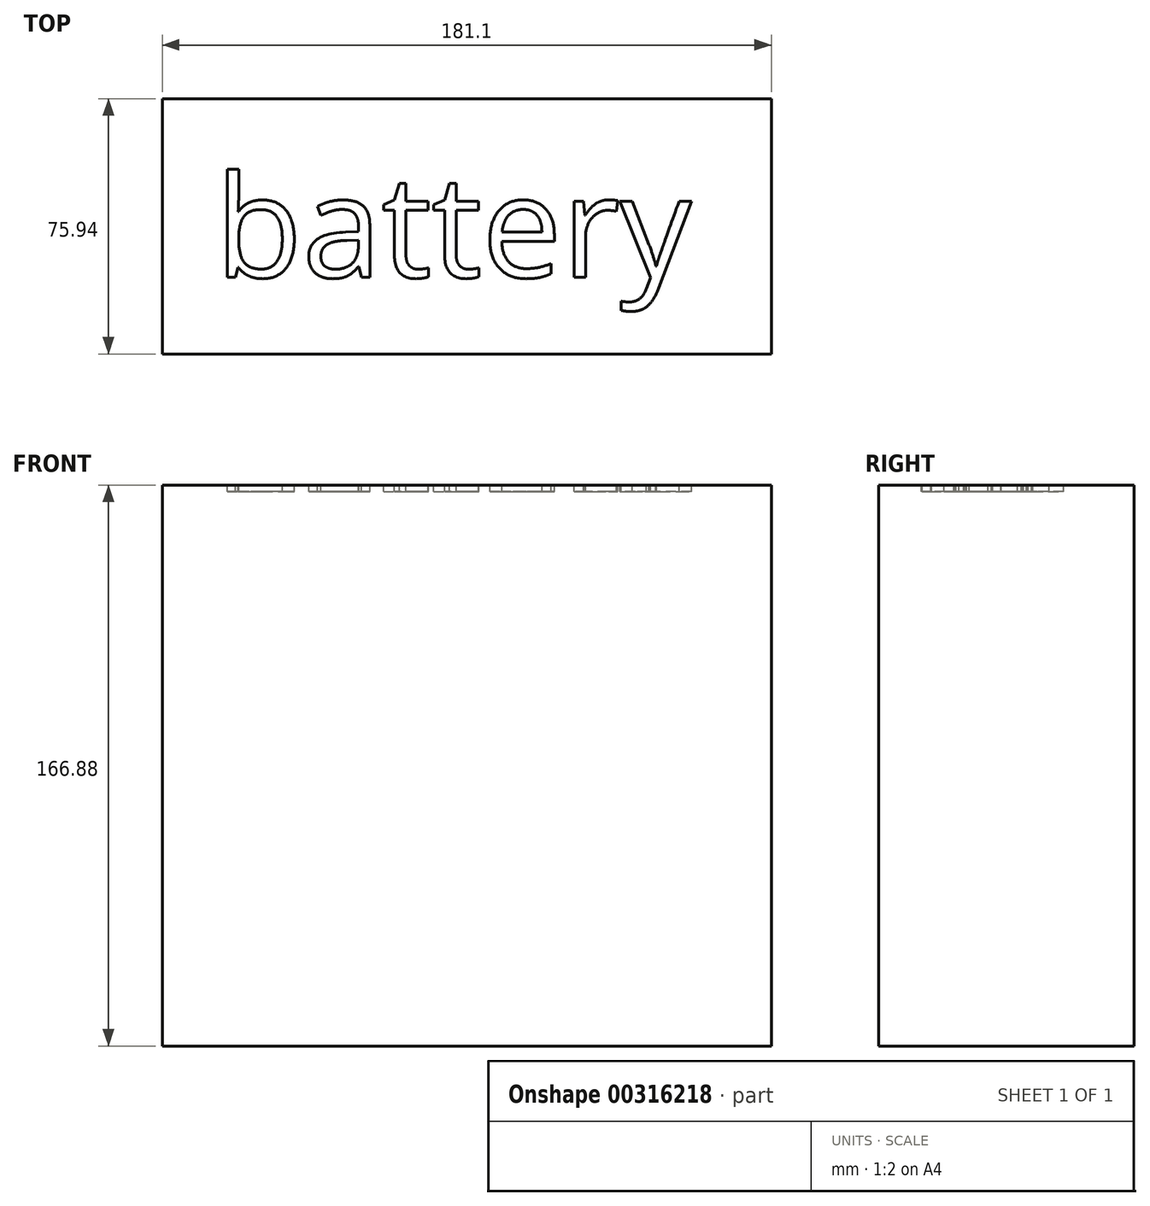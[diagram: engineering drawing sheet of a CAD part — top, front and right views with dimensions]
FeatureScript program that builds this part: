
annotation { "Feature Type Name" : "Feature", "Feature Type Description" : "" }
export const myFeature = defineFeature(function(context is Context, id is Id, definition is map)
    precondition{}
    {
        {
            var Q0;
            Q0=qCreatedBy(makeId("Top.planeOp"),FACE);
            var sketch = newSketch(context, id + "F0", { "sketchPlane" : qUnion([Q0])});
            skLineSegment(sketch, "E0.bottom", {"start": v(-90.55, 37.97) * mm, "end": v(90.55, 37.97) * mm});
            skLineSegment(sketch, "E0.top", {"start": v(-90.55, -37.97) * mm, "end": v(90.55, -37.97) * mm});
            skLineSegment(sketch, "E0.left", {"start": v(-90.55, 37.97) * mm, "end": v(-90.55, -37.97) * mm});
            skLineSegment(sketch, "E0.right", {"start": v(90.55, 37.97) * mm, "end": v(90.55, -37.97) * mm});
            skPoint(sketch, "E0.middle", {"position": v(0, 0) * mm});
            skSolve(sketch);
        }
        {
            var Q0;
            Q0 = qSketchRegion(id + "F0", true);
            extrude(context, id + "F1", {"entities" : qUnion([Q0]), "depth" : 166.88 * mm});
        }
        {
            var Q0;
            Q0=makeQuery(id+"F1.opExtrude","CAP_FACE",FACE,{"disambiguationData":[OSD([sQuery(id+"F0.wireOp",EDGE,"E0.bottom"),sQuery(id+"F0.wireOp",EDGE,"E0.top"),sQuery(id+"F0.wireOp",EDGE,"E0.left"),sQuery(id+"F0.wireOp",EDGE,"E0.right")])],"isStart":false});
            var sketch = newSketch(context, id + "F2", { "sketchPlane" : qUnion([Q0])});
            skLineSegment(sketch, "E1.0.0", {"start": v(-90.55, 37.97) * mm, "end": v(-90.55, -37.97) * mm});
            skLineSegment(sketch, "E1.0.1", {"start": v(-90.55, -37.97) * mm, "end": v(90.55, -37.97) * mm});
            skLineSegment(sketch, "E1.0.2", {"start": v(90.55, -37.97) * mm, "end": v(90.55, 37.97) * mm});
            skLineSegment(sketch, "E1.0.3", {"start": v(90.55, 37.97) * mm, "end": v(-90.55, 37.97) * mm});
            skText(sketch, "E2", { "text": "battery", "fontName": "OpenSans-Regular.ttf"});
            const initialGuessF2  = {"E2": [-0.07487, -0.0152, 1, 0, 0.03048]};
            skSetInitialGuess(sketch, initialGuessF2);
            skSolve(sketch);
        }
        {
            var Q0;
            Q0=makeQuery(id+"F2.imprint","IMPRINT",FACE,{"disambiguationData":[TD([[makeQuery(id+"F2.imprint","IMPRINT",EDGE,{"derivedFrom":sQuery(id+"F2.wireOp",EDGE,"E2.sketch_text.stroke-0")}),-1.0]])]});
            var Q1;
            Q1=makeQuery(id+"F2.imprint","IMPRINT",FACE,{"disambiguationData":[TD([[makeQuery(id+"F2.imprint","IMPRINT",EDGE,{"derivedFrom":sQuery(id+"F2.wireOp",EDGE,"E2.sketch_text.stroke-50")}),-1.0]])]});
            var Q2;
            Q2=makeQuery(id+"F2.imprint","IMPRINT",FACE,{"disambiguationData":[TD([[makeQuery(id+"F2.imprint","IMPRINT",EDGE,{"derivedFrom":sQuery(id+"F2.wireOp",EDGE,"E2.sketch_text.stroke-69")}),-1.0]])]});
            var Q3;
            Q3=makeQuery(id+"F2.imprint","IMPRINT",FACE,{"disambiguationData":[TD([[makeQuery(id+"F2.imprint","IMPRINT",EDGE,{"derivedFrom":sQuery(id+"F2.wireOp",EDGE,"E2.sketch_text.stroke-88")}),-1.0]])]});
            var Q4;
            Q4=makeQuery(id+"F2.imprint","IMPRINT",FACE,{"disambiguationData":[TD([[makeQuery(id+"F2.imprint","IMPRINT",EDGE,{"derivedFrom":sQuery(id+"F2.wireOp",EDGE,"E2.sketch_text.stroke-107")}),-1.0]])]});
            var Q5;
            Q5=makeQuery(id+"F2.imprint","IMPRINT",FACE,{"disambiguationData":[TD([[makeQuery(id+"F2.imprint","IMPRINT",EDGE,{"derivedFrom":sQuery(id+"F2.wireOp",EDGE,"E2.sketch_text.stroke-120")}),-1.0]])]});
            var Q6;
            Q6=makeQuery(id+"F2.imprint","IMPRINT",FACE,{"disambiguationData":[TD([[makeQuery(id+"F2.imprint","IMPRINT",EDGE,{"derivedFrom":sQuery(id+"F2.wireOp",EDGE,"E2.sketch_text.stroke-23")}),-1.0]])]});
            extrude(context, id + "F3", {"entities" : qUnion([Q0, Q1, Q2, Q3, Q4, Q5, Q6]), "operationType" : NewBodyOperationType.REMOVE, "oppositeDirection" : true, "depth" : 2 * mm});
        }
    });
